# Revit family: HERZ Strainer 4111
name_source: partatom
category: Rohrzubehör
units: mm (PartAtom-declared; Revit-internal decimal feet)

## family parameters
Arbeitsebenenbasiert = Nein
Beim Laden mit Abzugskörper schneiden = Nein
Bemaßung runder Anschluss = Durchmesser verwenden
Gemeinsam genutzt = Nein
Immer vertikal = Ja
OmniClass-Nummer = 23.65.55.14
OmniClass-Titel = Valves for Liquid Services
Teiletyp = Unterbricht

## types (1)
- HERZ Strainer 4111
    Application = For hot and cold water systems for fluids excluding acid and flammable fluids.
    Body = GG25
    Bonnet = GG25
    Filter (DN100-DN400) = AISI 304, mesh size 1500 μm
    Filter (DN50-DN80) = AISI 304, mesh size 600 μm
    Hersteller = HERZ Armaturen Ges.m.b.H.
    Max. operating temperature = 120 °C
    Medium = Heating water quality according ÖNORM H5195 or VDI-Standard 2035. The use of ethylene or propylene glycol in a mixing ratio 25-50% is allowed.
    Min. operating temperature = -10 °C
    PN = 1600000.0 Pa
    Plug = steel St37
    Plug sealing = copper
    Reinforcing frame = stainless steel
    SCRNCODE = 05;15;02
    SCRNSEQ = AWI;AWI_TYP="1011";2
    Seal = Klingerit
    URL = www.herzvalves.com
    Vorgabe-Ansicht = 0 mm  [stored 0 ft]
    W01 = 140.00°
    W02 = 45.00°

note: [stored X ft] marks values corroborated as IEEE doubles in the binary element streams (Revit-internal decimal feet)
